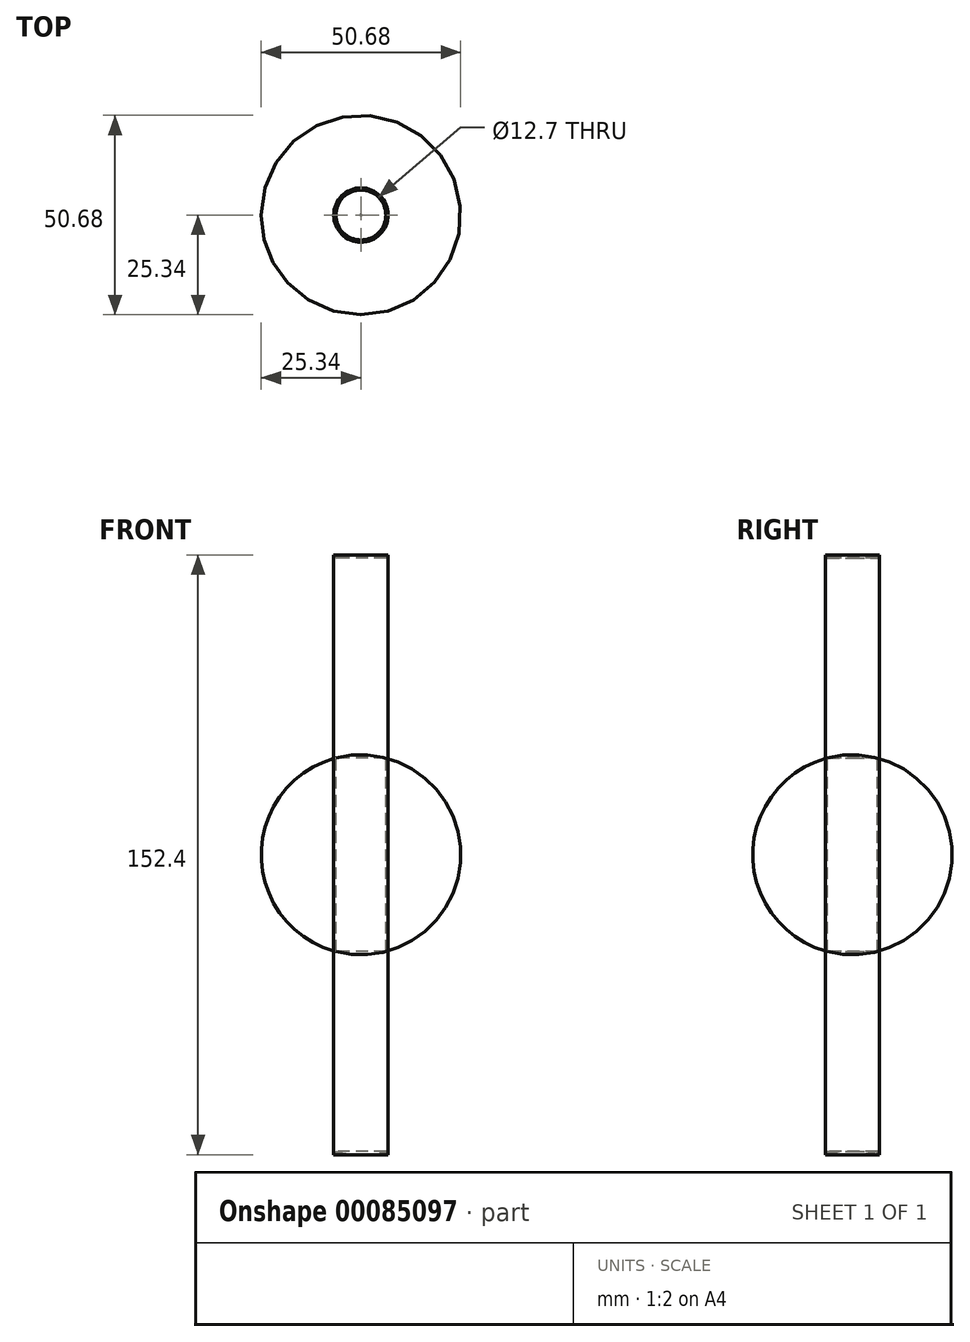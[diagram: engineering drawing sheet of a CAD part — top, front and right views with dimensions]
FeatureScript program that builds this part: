
annotation { "Feature Type Name" : "Feature", "Feature Type Description" : "" }
export const myFeature = defineFeature(function(context is Context, id is Id, definition is map)
    precondition{}
    {
        {
            var Q0;
            Q0=qCreatedBy(makeId("Front.planeOp"),FACE);
            var sketch = newSketch(context, id + "F0", { "sketchPlane" : qUnion([Q0])});
            skLineSegment(sketch, "E0.bottom", {"start": v(-6.35, -76.2) * mm, "end": v(6.35, -76.2) * mm});
            skLineSegment(sketch, "E0.top", {"start": v(-6.35, 76.2) * mm, "end": v(6.35, 76.2) * mm});
            skLineSegment(sketch, "E0.left", {"start": v(-6.35, -76.2) * mm, "end": v(-6.35, 76.2) * mm});
            skLineSegment(sketch, "E0.right", {"start": v(6.35, -76.2) * mm, "end": v(6.35, -26.2) * mm});
            skPoint(sketch, "E0.middle", {"position": v(0, 0) * mm});
            skLineSegment(sketch, "E1", {"start": v(-75.9, 25.4) * mm, "end": v(82.63, 25.4) * mm, "construction": true});
            skLineSegment(sketch, "E2", {"start": v(-75.9, -25.4) * mm, "end": v(79.26, -25.4) * mm, "construction": true});
            skLineSegment(sketch, "E3", {"start": v(25.4, 76.2) * mm, "end": v(25.4, -77.34) * mm, "construction": true});
            skArc(sketch, "E4", {"start": v(0, -25.4) * mm, "mid": v(0.06, -25.4) * mm, "end": v(0.12, -25.4) * mm});
            skArc(sketch, "E5.MirrorCS", {"start": v(0, 76.2) * mm, "mid": v(25.26, 54) * mm, "end": v(6.35, 26.2) * mm});
            skLineSegment(sketch, "E6", {"start": v(0, 90.31) * mm, "end": v(0, -110.49) * mm, "construction": true});
            skArc(sketch, "E7.trimOffspring", {"start": v(0.12, 25.4) * mm, "mid": v(0.06, 25.4) * mm, "end": v(0, 25.4) * mm});
            skArc(sketch, "E8.trimOffspring", {"start": v(6.35, -24.6) * mm, "mid": v(25.46, 0) * mm, "end": v(6.35, 24.6) * mm});
            skArc(sketch, "E9.trimOffspring", {"start": v(6.35, -26.2) * mm, "mid": v(25.26, -54) * mm, "end": v(0, -76.2) * mm});
            skLineSegment(sketch, "E10.trimOffspring", {"start": v(6.35, -25.4) * mm, "end": v(6.35, 76.2) * mm});
            skSolve(sketch);
        }
        {
            var Q0;
            {var subQ0=sQuery(id+"F0.wireOp",EDGE,"E9.trimOffspring");var subQ1=sQuery(id+"F0.wireOp",EDGE,"E0.right");var subQ2=makeQuery(id+"F0.imprint","INTERSECT",VERTEX,{"disambiguationData":[OD(0.0)],"derivedFrom":[subQ1,subQ0]});Q0=makeQuery(id+"F0.imprint","IMPRINT",FACE,{"disambiguationData":[TD([[makeQuery(id+"F0.imprint","IMPRINT",EDGE,{"disambiguationData":[TD([[subQ2,1.0]])],"derivedFrom":subQ1}),-1.0]])]});}
            var Q1;
            {var subQ0=sQuery(id+"F0.wireOp",EDGE,"E10.trimOffspring");var subQ1=sQuery(id+"F0.wireOp",EDGE,"E5.MirrorCS");var subQ2=makeQuery(id+"F0.imprint","INTERSECT",VERTEX,{"disambiguationData":[OD(0.0)],"derivedFrom":[subQ1,subQ0]});Q1=makeQuery(id+"F0.imprint","IMPRINT",FACE,{"disambiguationData":[TD([[makeQuery(id+"F0.imprint","IMPRINT",EDGE,{"disambiguationData":[TD([[subQ2,1.0]])],"derivedFrom":subQ1}),-1.0]])]});}
            var Q2;
            {var subQ0=sQuery(id+"F0.wireOp",EDGE,"E8.trimOffspring");Q2=makeQuery(id+"F0.imprint","IMPRINT",FACE,{"disambiguationData":[TD([[makeQuery(id+"F0.imprint","IMPRINT",EDGE,{"derivedFrom":subQ0}),1.0]])]});}
            var Q3;
            {var subQ0=sQuery(id+"F0.wireOp",EDGE,"E0.right");var subQ1=sQuery(id+"F0.wireOp",EDGE,"E0.bottom");var subQ2=makeQuery(id+"F0.imprint","INTERSECT",VERTEX,{"derivedFrom":[subQ1,subQ0]});Q3=makeQuery(id+"F0.imprint","IMPRINT",FACE,{"disambiguationData":[TD([[makeQuery(id+"F0.imprint","IMPRINT",EDGE,{"disambiguationData":[TD([[subQ2,1.0]])],"derivedFrom":subQ1}),1.0]])]});}
            var Q4;
            {var subQ0=sQuery(id+"F0.wireOp",EDGE,"E10.trimOffspring");var subQ1=sQuery(id+"F0.wireOp",EDGE,"E0.top");var subQ2=makeQuery(id+"F0.imprint","INTERSECT",VERTEX,{"derivedFrom":[subQ1,subQ0]});Q4=makeQuery(id+"F0.imprint","IMPRINT",FACE,{"disambiguationData":[TD([[makeQuery(id+"F0.imprint","IMPRINT",EDGE,{"disambiguationData":[TD([[subQ2,1.0]])],"derivedFrom":subQ1}),-1.0]])]});}
            var Q5;
            Q5=sQuery(id+"F0.wireOp",EDGE,"E6");
            revolve(context, id + "F1", {"entities" : qUnion([Q0, Q1, Q2, Q3, Q4]), "axis" : qUnion([Q5]), "revolveType" : RevolveType.FULL});
        }
        {
            var Q0;
            Q0=qCreatedBy(makeId("Top.planeOp"),FACE);
            var sketch = newSketch(context, id + "F2", { "sketchPlane" : qUnion([Q0])});
            skCircle(sketch, "E11", {"center": v(0, 0) * mm, "radius": 6.9 * mm});
            skSolve(sketch);
        }
        {
            var Q0;
            Q0 = qSketchRegion(id + "F2", true);
            extrude(context, id + "F3", {"entities" : qUnion([Q0]), "endBound" : BoundingType.SYMMETRIC, "depth" : 152.4 * mm});
        }
    });
